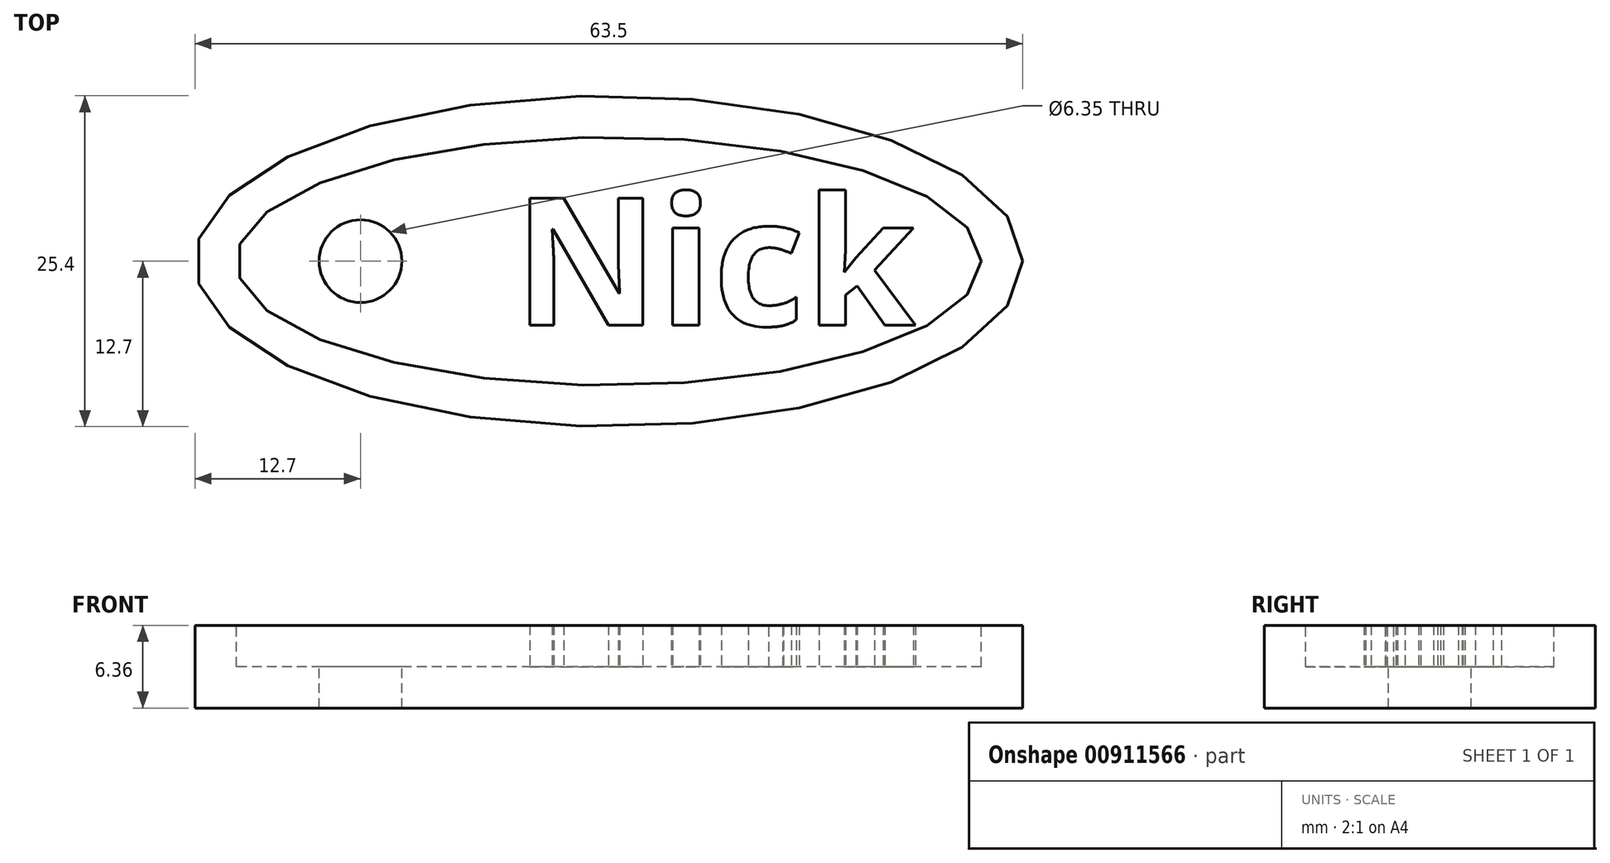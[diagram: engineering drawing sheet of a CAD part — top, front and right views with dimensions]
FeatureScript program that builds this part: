
annotation { "Feature Type Name" : "Feature", "Feature Type Description" : "" }
export const myFeature = defineFeature(function(context is Context, id is Id, definition is map)
    precondition{}
    {
        {
            var Q0;
            Q0=qCreatedBy(makeId("Top.planeOp"),FACE);
            var sketch = newSketch(context, id + "F0", { "sketchPlane" : qUnion([Q0])});
            skEllipse(sketch, "E0", {"center": v(0, 0) * mm, "majorRadius": 31.75 * mm, "minorRadius": 12.7 * mm, "majorAxis": v(1, 0)});
            skSolve(sketch);
        }
        {
            var Q0;
            Q0 = qSketchRegion(id + "F0", true);
            extrude(context, id + "F1", {"entities" : qUnion([Q0]), "endBound" : BoundingType.SYMMETRIC, "depth" : 6.35 * mm, "offsetDistance" : 25.4 * mm});
        }
        {
            var Q0;
            Q0=makeQuery(id+"F1.opExtrude","CAP_FACE",FACE,{"disambiguationData":[OSD([sQuery(id+"F0.wireOp",EDGE,"E0")])],"isStart":false});
            var sketch = newSketch(context, id + "F2", { "sketchPlane" : qUnion([Q0])});
            skEllipse(sketch, "E1", {"center": v(0, 0) * mm, "majorRadius": 28.58 * mm, "minorRadius": 9.53 * mm, "majorAxis": v(1, 0)});
            skSolve(sketch);
        }
        {
            var Q0;
            Q0 = qSketchRegion(id + "F2", true);
            extrude(context, id + "F3", {"entities" : qUnion([Q0]), "operationType" : NewBodyOperationType.REMOVE, "oppositeDirection" : true, "depth" : 3.17 * mm, "offsetDistance" : 25.4 * mm});
        }
        {
            var Q0;
            Q0=makeQuery(id+"F3.boolean.opBoolean","COPY",FACE,{"derivedFrom":makeQuery(id+"F3.opExtrude","CAP_FACE",FACE,{"disambiguationData":[OSD([sQuery(id+"F2.wireOp",EDGE,"E1")])],"isStart":false})});
            var sketch = newSketch(context, id + "F4", { "sketchPlane" : qUnion([Q0])});
            skText(sketch, "E2", { "text": "Nick", "fontName": "OpenSans-Bold.ttf"});
            const initialGuessF4  = {"E2": [-0.0073, -0.00493, 1, 0, 0.00986]};
            skSetInitialGuess(sketch, initialGuessF4);
            skSolve(sketch);
        }
        {
            var Q0;
            Q0 = qSketchRegion(id + "F4", true);
            extrude(context, id + "F5", {"entities" : qUnion([Q0]), "operationType" : NewBodyOperationType.ADD, "depth" : 3.17 * mm, "offsetDistance" : 25.4 * mm});
        }
        {
            var Q0;
            Q0=makeQuery(id+"F3.boolean.opBoolean","COPY",FACE,{"derivedFrom":makeQuery(id+"F3.opExtrude","CAP_FACE",FACE,{"disambiguationData":[OSD([sQuery(id+"F2.wireOp",EDGE,"E1")])],"isStart":false})});
            var sketch = newSketch(context, id + "F6", { "sketchPlane" : qUnion([Q0])});
            skCircle(sketch, "E3", {"center": v(-19.05, 0) * mm, "radius": 3.18 * mm});
            skSolve(sketch);
        }
        {
            var Q0;
            Q0 = qSketchRegion(id + "F6", true);
            extrude(context, id + "F7", {"entities" : qUnion([Q0]), "operationType" : NewBodyOperationType.REMOVE, "endBound" : BoundingType.THROUGH_ALL, "oppositeDirection" : true, "depth" : 25.4 * mm, "offsetDistance" : 25.4 * mm});
        }
    });
